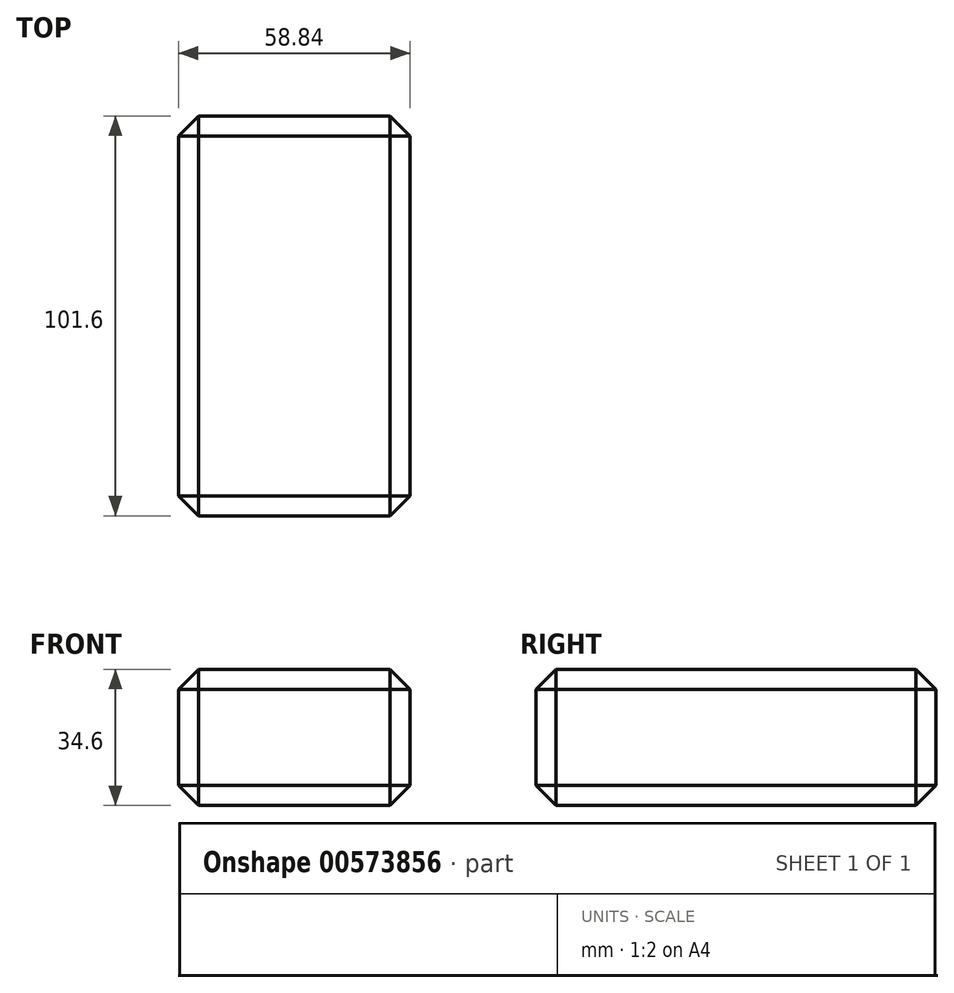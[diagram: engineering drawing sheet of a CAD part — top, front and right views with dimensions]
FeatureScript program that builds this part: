
annotation { "Feature Type Name" : "Feature", "Feature Type Description" : "" }
export const myFeature = defineFeature(function(context is Context, id is Id, definition is map)
    precondition{}
    {
        {
            var Q0;
            Q0=qCreatedBy(makeId("Front.planeOp"),FACE);
            var sketch = newSketch(context, id + "F0", { "sketchPlane" : qUnion([Q0])});
            skLineSegment(sketch, "E0.bottom", {"start": v(0, 0) * mm, "end": v(-58.84, 0) * mm});
            skLineSegment(sketch, "E0.top", {"start": v(0, 34.6) * mm, "end": v(-58.84, 34.6) * mm});
            skLineSegment(sketch, "E0.left", {"start": v(0, 0) * mm, "end": v(0, 34.6) * mm});
            skLineSegment(sketch, "E0.right", {"start": v(-58.84, 0) * mm, "end": v(-58.84, 34.6) * mm});
            skSolve(sketch);
        }
        {
            var Q0;
            Q0=makeQuery(id+"F0.imprint","IMPRINT",FACE,{"disambiguationData":[TD([[makeQuery(id+"F0.imprint","IMPRINT",EDGE,{"derivedFrom":sQuery(id+"F0.wireOp",EDGE,"E0.bottom")}),-1.0]])]});
            extrude(context, id + "F1", {"entities" : qUnion([Q0]), "depth" : 101.6 * mm, "offsetDistance" : 25.4 * mm});
        }
        {
            var Q0;
            Q0=makeQuery(id+"F1.opExtrude","CAP_FACE",FACE,{"disambiguationData":[OSD([sQuery(id+"F0.wireOp",EDGE,"E0.bottom"),sQuery(id+"F0.wireOp",EDGE,"E0.top"),sQuery(id+"F0.wireOp",EDGE,"E0.left"),sQuery(id+"F0.wireOp",EDGE,"E0.right")])],"isStart":false});
            var Q1;
            Q1=makeQuery(id+"F1.opExtrude","CAP_FACE",FACE,{"disambiguationData":[OSD([sQuery(id+"F0.wireOp",EDGE,"E0.bottom"),sQuery(id+"F0.wireOp",EDGE,"E0.top"),sQuery(id+"F0.wireOp",EDGE,"E0.left"),sQuery(id+"F0.wireOp",EDGE,"E0.right")])],"isStart":true});
            var Q2;
            Q2=makeQuery(id+"F1.opExtrude","SWEPT_FACE",FACE,{"disambiguationData":[OSD([sQuery(id+"F0.wireOp",EDGE,"E0.bottom")])]});
            var Q3;
            Q3=makeQuery(id+"F1.opExtrude","SWEPT_FACE",FACE,{"disambiguationData":[OSD([sQuery(id+"F0.wireOp",EDGE,"E0.right")])]});
            var Q4;
            Q4=makeQuery(id+"F1.opExtrude","SWEPT_FACE",FACE,{"disambiguationData":[OSD([sQuery(id+"F0.wireOp",EDGE,"E0.left")])]});
            chamfer(context, id + "F2", {"entities" : qUnion([Q0, Q1, Q2, Q3, Q4]), "width" : 5.08 * mm, "tangentPropagation" : true});
        }
    });
